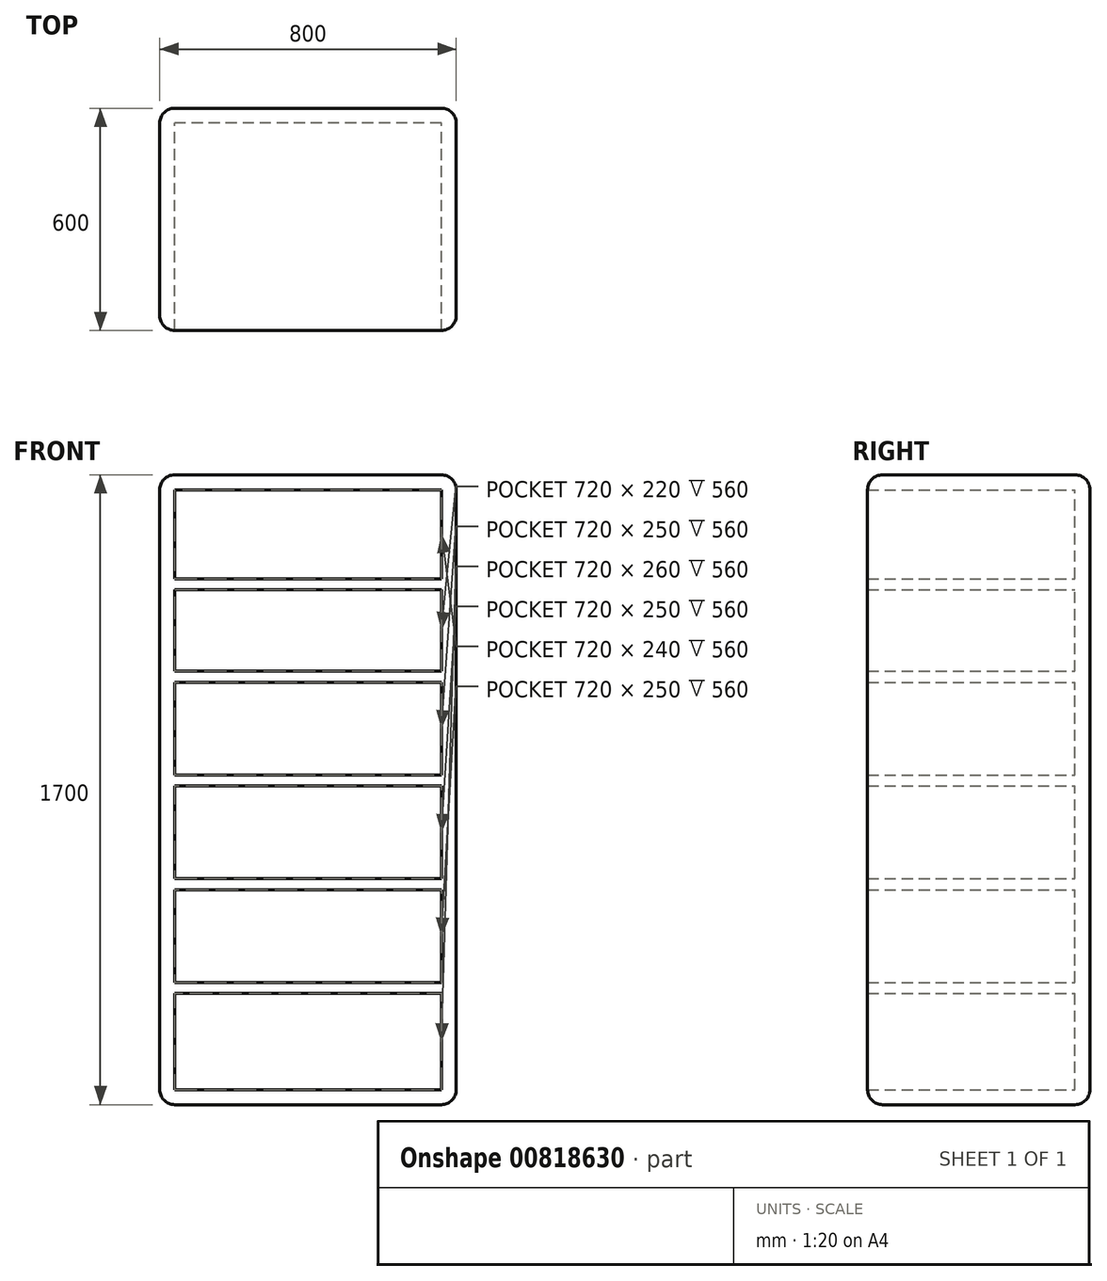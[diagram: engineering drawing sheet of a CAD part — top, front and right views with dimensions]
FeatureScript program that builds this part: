
annotation { "Feature Type Name" : "Feature", "Feature Type Description" : "" }
export const myFeature = defineFeature(function(context is Context, id is Id, definition is map)
    precondition{}
    {
        {
            var Q0;
            Q0=qCreatedBy(makeId("Front.planeOp"),FACE);
            var sketch = newSketch(context, id + "F0", { "sketchPlane" : qUnion([Q0])});
            skLineSegment(sketch, "E0.bottom", {"start": v(400, -850) * mm, "end": v(-400, -850) * mm});
            skLineSegment(sketch, "E0.top", {"start": v(400, 850) * mm, "end": v(-400, 850) * mm});
            skLineSegment(sketch, "E0.left", {"start": v(400, -850) * mm, "end": v(400, 850) * mm});
            skLineSegment(sketch, "E0.right", {"start": v(-400, -850) * mm, "end": v(-400, 850) * mm});
            skPoint(sketch, "E0.middle", {"position": v(0, 0) * mm});
            skSolve(sketch);
        }
        {
            var Q0;
            Q0 = qSketchRegion(id + "F0", true);
            extrude(context, id + "F1", {"entities" : qUnion([Q0]), "depth" : 600 * mm, "offsetDistance" : 25 * mm});
        }
        {
            var Q0;
            Q0=makeQuery(id+"F1.opExtrude","CAP_FACE",FACE,{"disambiguationData":[OSD([sQuery(id+"F0.wireOp",EDGE,"E0.bottom"),sQuery(id+"F0.wireOp",EDGE,"E0.top"),sQuery(id+"F0.wireOp",EDGE,"E0.left"),sQuery(id+"F0.wireOp",EDGE,"E0.right")])],"isStart":false});
            shell(context, id + "F2", {"entities" : qUnion([Q0]), "thickness" : 40 * mm});
        }
        {
            var Q0;
            Q0=makeQuery(id+"F2.opShell","OFFSET_FACE",FACE,{"disambiguationData":[OSD([sQuery(id+"F0.wireOp",EDGE,"E0.bottom"),sQuery(id+"F0.wireOp",EDGE,"E0.top"),sQuery(id+"F0.wireOp",EDGE,"E0.left"),sQuery(id+"F0.wireOp",EDGE,"E0.right")])]});
            var sketch = newSketch(context, id + "F3", { "sketchPlane" : qUnion([Q0])});
            skLineSegment(sketch, "E1", {"start": v(-360, -810) * mm, "end": v(-360, -270) * mm});
            skLineSegment(sketch, "E2.bottom", {"start": v(-360, -270) * mm, "end": v(360, -270) * mm});
            skLineSegment(sketch, "E2.top", {"start": v(-360, -240) * mm, "end": v(360, -240) * mm});
            skLineSegment(sketch, "E2.left", {"start": v(-360, -270) * mm, "end": v(-360, -240) * mm});
            skLineSegment(sketch, "E2.right", {"start": v(360, -270) * mm, "end": v(360, -240) * mm});
            skSolve(sketch);
        }
        {
            var Q0;
            Q0=makeQuery(id+"F3.imprint","IMPRINT",FACE,{"disambiguationData":[TD([[makeQuery(id+"F3.imprint","IMPRINT",EDGE,{"derivedFrom":sQuery(id+"F3.wireOp",EDGE,"E2.bottom")}),1.0]])]});
            extrude(context, id + "F4", {"entities" : qUnion([Q0]), "operationType" : NewBodyOperationType.ADD, "depth" : 560 * mm, "offsetDistance" : 25 * mm});
        }
        {
            var Q0;
            Q0=makeQuery(id+"F1.opExtrude","CAP_EDGE",EDGE,{"disambiguationData":[OSD([sQuery(id+"F0.wireOp",EDGE,"E0.right")])],"isStart":false});
            var Q1;
            Q1=makeQuery(id+"F1.opExtrude","SWEPT_EDGE",EDGE,{"disambiguationData":[OSD([sQuery(id+"F0.wireOp",EDGE,"E0.top"),sQuery(id+"F0.wireOp",EDGE,"E0.right")])]});
            var Q2;
            Q2=makeQuery(id+"F1.opExtrude","CAP_EDGE",EDGE,{"disambiguationData":[OSD([sQuery(id+"F0.wireOp",EDGE,"E0.top")])],"isStart":false});
            var Q3;
            Q3=makeQuery(id+"F1.opExtrude","SWEPT_EDGE",EDGE,{"disambiguationData":[OSD([sQuery(id+"F0.wireOp",EDGE,"E0.top"),sQuery(id+"F0.wireOp",EDGE,"E0.left")])]});
            var Q4;
            Q4=makeQuery(id+"F1.opExtrude","CAP_EDGE",EDGE,{"disambiguationData":[OSD([sQuery(id+"F0.wireOp",EDGE,"E0.top")])],"isStart":true});
            var Q5;
            Q5=makeQuery(id+"F1.opExtrude","CAP_EDGE",EDGE,{"disambiguationData":[OSD([sQuery(id+"F0.wireOp",EDGE,"E0.right")])],"isStart":true});
            var Q6;
            Q6=makeQuery(id+"F1.opExtrude","CAP_EDGE",EDGE,{"disambiguationData":[OSD([sQuery(id+"F0.wireOp",EDGE,"E0.left")])],"isStart":true});
            var Q7;
            Q7=makeQuery(id+"F1.opExtrude","CAP_EDGE",EDGE,{"disambiguationData":[OSD([sQuery(id+"F0.wireOp",EDGE,"E0.bottom")])],"isStart":true});
            var Q8;
            Q8=makeQuery(id+"F1.opExtrude","SWEPT_EDGE",EDGE,{"disambiguationData":[OSD([sQuery(id+"F0.wireOp",EDGE,"E0.bottom"),sQuery(id+"F0.wireOp",EDGE,"E0.right")])]});
            var Q9;
            Q9=makeQuery(id+"F1.opExtrude","SWEPT_FACE",FACE,{"disambiguationData":[OSD([sQuery(id+"F0.wireOp",EDGE,"E0.bottom")])]});
            var Q10;
            Q10=makeQuery(id+"F1.opExtrude","CAP_EDGE",EDGE,{"disambiguationData":[OSD([sQuery(id+"F0.wireOp",EDGE,"E0.left")])],"isStart":false});
            fillet(context, id + "F5", {"entities" : qUnion([Q0, Q1, Q2, Q3, Q4, Q5, Q6, Q7, Q8, Q9, Q10]), "radius" : 40 * mm, "tangentPropagation" : true, "allowEdgeOverflow" : false});
        }
        {
            var Q0;
            {var subQ0=sQuery(id+"F0.wireOp",EDGE,"E0.top");var subQ1=sQuery(id+"F0.wireOp",EDGE,"E0.left");var subQ2=sQuery(id+"F0.wireOp",EDGE,"E0.right");Q0=makeQuery(id+"F4.boolean.opBoolean","SPLIT",FACE,{"disambiguationData":[TD([makeQuery(id+"F2.opShell","OFFSET_FACE",FACE,{"disambiguationData":[OSD([subQ0])]})])],"derivedFrom":makeQuery(id+"F2.opShell","OFFSET_FACE",FACE,{"disambiguationData":[OSD([sQuery(id+"F0.wireOp",EDGE,"E0.bottom"),subQ0,subQ1,subQ2])]})});}
            var sketch = newSketch(context, id + "F6", { "sketchPlane" : qUnion([Q0])});
            skLineSegment(sketch, "E3", {"start": v(-360, 810) * mm, "end": v(-360, -240) * mm});
            skLineSegment(sketch, "E4", {"start": v(-360, -240) * mm, "end": v(-360, 20.5) * mm});
            skLineSegment(sketch, "E5", {"start": v(360, -240) * mm, "end": v(360, 10) * mm});
            skLineSegment(sketch, "E6.bottom", {"start": v(360, 10) * mm, "end": v(-360, 10) * mm});
            skLineSegment(sketch, "E6.top", {"start": v(360, 40) * mm, "end": v(-360, 40) * mm});
            skLineSegment(sketch, "E6.left", {"start": v(360, 10) * mm, "end": v(360, 40) * mm});
            skLineSegment(sketch, "E6.right", {"start": v(-360, 10) * mm, "end": v(-360, 40) * mm});
            skSolve(sketch);
        }
        {
            var Q0;
            {var subQ0=sQuery(id+"F6.wireOp",EDGE,"E6.bottom");Q0=makeQuery(id+"F6.imprint","IMPRINT",FACE,{"disambiguationData":[TD([[makeQuery(id+"F6.imprint","IMPRINT",EDGE,{"derivedFrom":subQ0}),-1.0]])]});}
            extrude(context, id + "F7", {"entities" : qUnion([Q0]), "operationType" : NewBodyOperationType.ADD, "depth" : 560 * mm, "offsetDistance" : 25 * mm});
        }
        {
            var Q0;
            {var subQ0=sQuery(id+"F0.wireOp",EDGE,"E0.bottom");var subQ1=sQuery(id+"F0.wireOp",EDGE,"E0.left");var subQ2=sQuery(id+"F0.wireOp",EDGE,"E0.right");Q0=makeQuery(id+"F4.boolean.opBoolean","SPLIT",FACE,{"disambiguationData":[TD([makeQuery(id+"F2.opShell","OFFSET_FACE",FACE,{"disambiguationData":[OSD([subQ0])]})])],"derivedFrom":makeQuery(id+"F2.opShell","OFFSET_FACE",FACE,{"disambiguationData":[OSD([subQ0,sQuery(id+"F0.wireOp",EDGE,"E0.top"),subQ1,subQ2])]})});}
            var sketch = newSketch(context, id + "F8", { "sketchPlane" : qUnion([Q0])});
            skLineSegment(sketch, "E7", {"start": v(-360, -810) * mm, "end": v(-360, -270) * mm});
            skLineSegment(sketch, "E8", {"start": v(360, -270) * mm, "end": v(360, -520) * mm});
            skLineSegment(sketch, "E9.bottom", {"start": v(360, -520) * mm, "end": v(-360, -520) * mm});
            skLineSegment(sketch, "E9.top", {"start": v(360, -550) * mm, "end": v(-360, -550) * mm});
            skLineSegment(sketch, "E9.left", {"start": v(360, -520) * mm, "end": v(360, -550) * mm});
            skLineSegment(sketch, "E9.right", {"start": v(-360, -520) * mm, "end": v(-360, -550) * mm});
            skSolve(sketch);
        }
        {
            var Q0;
            Q0=makeQuery(id+"F8.imprint","IMPRINT",FACE,{"disambiguationData":[TD([[makeQuery(id+"F8.imprint","IMPRINT",EDGE,{"derivedFrom":sQuery(id+"F8.wireOp",EDGE,"E9.bottom")}),1.0]])]});
            extrude(context, id + "F9", {"entities" : qUnion([Q0]), "operationType" : NewBodyOperationType.ADD, "depth" : 560 * mm, "offsetDistance" : 25 * mm});
        }
        {
            var Q0;
            {var subQ0=sQuery(id+"F0.wireOp",EDGE,"E0.top");var subQ1=makeQuery(id+"F2.opShell","OFFSET_FACE",FACE,{"disambiguationData":[OSD([subQ0])]});var subQ2=sQuery(id+"F0.wireOp",EDGE,"E0.left");var subQ4=sQuery(id+"F0.wireOp",EDGE,"E0.right");Q0=makeQuery(id+"F7.boolean.opBoolean","SPLIT",FACE,{"disambiguationData":[TD([subQ1])],"derivedFrom":makeQuery(id+"F4.boolean.opBoolean","SPLIT",FACE,{"disambiguationData":[TD([subQ1])],"derivedFrom":makeQuery(id+"F2.opShell","OFFSET_FACE",FACE,{"disambiguationData":[OSD([sQuery(id+"F0.wireOp",EDGE,"E0.bottom"),subQ0,subQ2,subQ4])]})})});}
            var sketch = newSketch(context, id + "F10", { "sketchPlane" : qUnion([Q0])});
            skLineSegment(sketch, "E10", {"start": v(360, 40) * mm, "end": v(360, 290) * mm});
            skLineSegment(sketch, "E11", {"start": v(360, 290) * mm, "end": v(360, 540) * mm});
            skLineSegment(sketch, "E12.bottom", {"start": v(360, 290) * mm, "end": v(-360, 290) * mm});
            skLineSegment(sketch, "E12.top", {"start": v(360, 320) * mm, "end": v(-360, 320) * mm});
            skLineSegment(sketch, "E12.left", {"start": v(360, 290) * mm, "end": v(360, 320) * mm});
            skLineSegment(sketch, "E12.right", {"start": v(-360, 290) * mm, "end": v(-360, 320) * mm});
            skLineSegment(sketch, "E13.bottom", {"start": v(360, 540) * mm, "end": v(-360, 540) * mm});
            skLineSegment(sketch, "E13.top", {"start": v(360, 570) * mm, "end": v(-360, 570) * mm});
            skLineSegment(sketch, "E13.left", {"start": v(360, 540) * mm, "end": v(360, 570) * mm});
            skLineSegment(sketch, "E13.right", {"start": v(-360, 540) * mm, "end": v(-360, 570) * mm});
            skSolve(sketch);
        }
        {
            var Q0;
            Q0=makeQuery(id+"F10.imprint","IMPRINT",FACE,{"disambiguationData":[TD([[makeQuery(id+"F10.imprint","IMPRINT",EDGE,{"derivedFrom":sQuery(id+"F10.wireOp",EDGE,"E12.bottom")}),-1.0]])]});
            var Q1;
            Q1=makeQuery(id+"F10.imprint","IMPRINT",FACE,{"disambiguationData":[TD([[makeQuery(id+"F10.imprint","IMPRINT",EDGE,{"derivedFrom":sQuery(id+"F10.wireOp",EDGE,"E13.bottom")}),-1.0]])]});
            extrude(context, id + "F11", {"entities" : qUnion([Q0, Q1]), "operationType" : NewBodyOperationType.ADD, "depth" : 560 * mm, "offsetDistance" : 25 * mm});
        }
    });
